# Revit family: väggbasket_fast
name_source: partatom
category: Generic Models
revit_build: Autodesk Revit 2017 (Build: 20160225_1515(x64)
units: mm (PartAtom-declared; Revit-internal decimal feet)

## family parameters
Always vertical = Yes
Can host rebar = No
Cut with Voids When Loaded = No
Part Type = Normal
Room Calculation Point = No
Round Connector Dimension = Use Diameter
Shared = No
Work Plane-Based = No

## types (2) — shared parameters
Manufacturer = Saxi Vägg AB
URL = www.saxi.se
bredd_tavla = 1200 mm
hojd_tavla = 900 mm  [stored 2.95276 ft]

## per-type parameters (varying)
| type | Height | Model |
| Saxi Väggbasket Junior | 2600 mm  [stored 8.53018 ft] | Väggbasket Auto 1800x1050 |
| Saxi Väggbasket Senior | 3050 mm  [stored 10.0066 ft] | Väggbasket Fast 800 |

note: [stored X ft] marks values corroborated as IEEE doubles in the binary element streams (Revit-internal decimal feet)

## geometry (parser evidence)
native form markers: Sweep x16
no freeform markers — native parametric forms only
